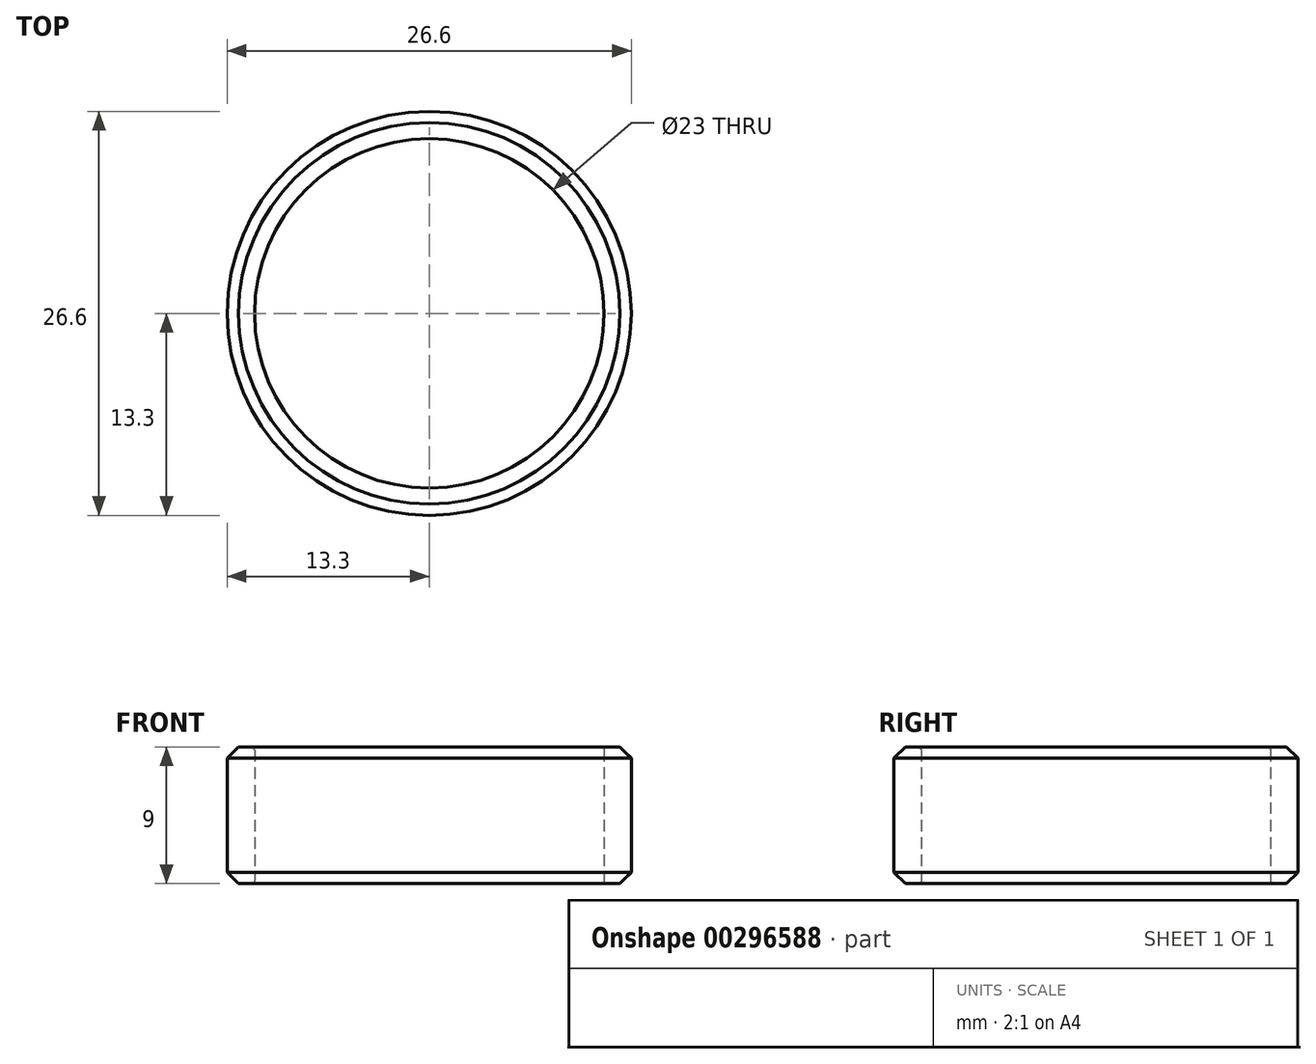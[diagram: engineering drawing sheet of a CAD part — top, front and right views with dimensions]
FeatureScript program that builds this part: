
annotation { "Feature Type Name" : "Feature", "Feature Type Description" : "" }
export const myFeature = defineFeature(function(context is Context, id is Id, definition is map)
    precondition{}
    {
        {
            var Q0;
            Q0=qCreatedBy(makeId("Top.planeOp"),FACE);
            var sketch = newSketch(context, id + "F0", { "sketchPlane" : qUnion([Q0])});
            skCircle(sketch, "E0", {"center": v(0, 0) * mm, "radius": 11.5 * mm});
            skCircle(sketch, "E1.0", {"center": v(0, 0) * mm, "radius": 13.3 * mm});
            skSolve(sketch);
        }
        {
            var Q0;
            Q0=makeQuery(id+"F0.imprint","IMPRINT",FACE,{"disambiguationData":[TD([[makeQuery(id+"F0.imprint","IMPRINT",EDGE,{"derivedFrom":sQuery(id+"F0.wireOp",EDGE,"E0")}),-1.0]])]});
            extrude(context, id + "F1", {"entities" : qUnion([Q0]), "depth" : 9 * mm});
        }
        {
            var Q0;
            Q0=makeQuery(id+"F1.opExtrude","CAP_EDGE",EDGE,{"disambiguationData":[OSD([sQuery(id+"F0.wireOp",EDGE,"E1.0")])],"isStart":false});
            var Q1;
            Q1=makeQuery(id+"F1.opExtrude","CAP_EDGE",EDGE,{"disambiguationData":[OSD([sQuery(id+"F0.wireOp",EDGE,"E1.0")])],"isStart":true});
            chamfer(context, id + "F2", {"entities" : qUnion([Q0, Q1]), "width" : .75 * mm, "tangentPropagation" : true});
        }
        {
            var Q0;
            Q0=makeQuery(id+"F1.opExtrude","CAP_EDGE",EDGE,{"disambiguationData":[OSD([sQuery(id+"F0.wireOp",EDGE,"E0")])],"isStart":false});
            fillet(context, id + "F3", {"entities" : qUnion([Q0]), "radius" : .2 * mm, "tangentPropagation" : true, "allowEdgeOverflow" : false});
        }
        {
            var Q0;
            Q0=makeQuery(id+"F1.opExtrude","SWEPT_FACE",FACE,{"disambiguationData":[OSD([sQuery(id+"F0.wireOp",EDGE,"E0")])]});
            fillet(context, id + "F4", {"entities" : qUnion([Q0]), "radius" : .2 * mm, "tangentPropagation" : true, "allowEdgeOverflow" : false});
        }
    });
